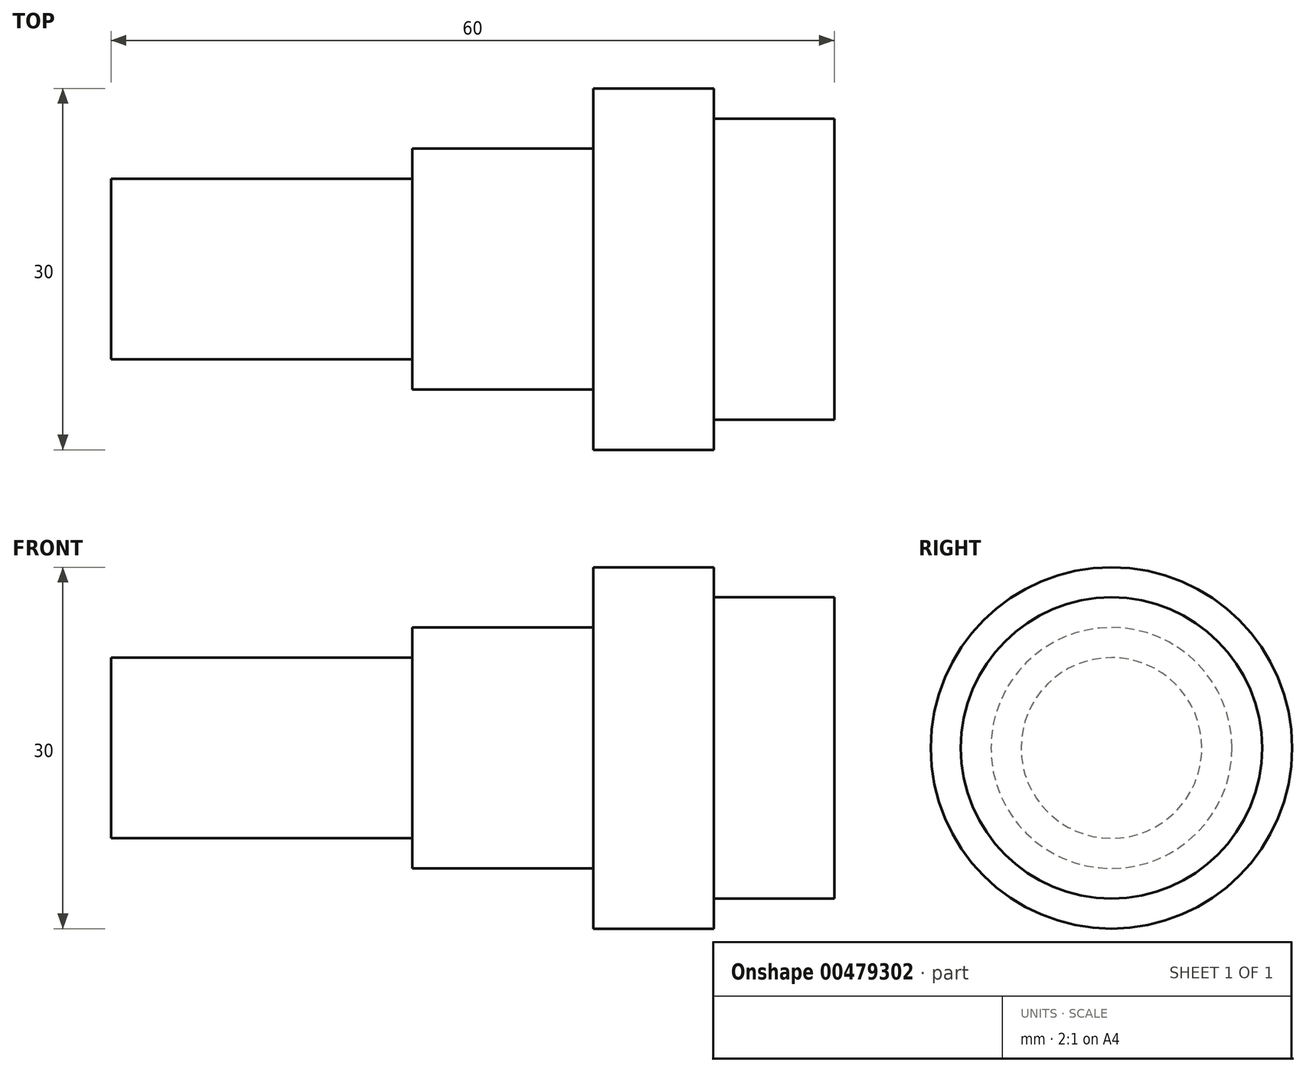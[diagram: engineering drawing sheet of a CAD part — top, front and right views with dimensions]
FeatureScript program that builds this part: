
annotation { "Feature Type Name" : "Feature", "Feature Type Description" : "" }
export const myFeature = defineFeature(function(context is Context, id is Id, definition is map)
    precondition{}
    {
        {
            var Q0;
            Q0=qCreatedBy(makeId("Right.planeOp"),FACE);
            var sketch = newSketch(context, id + "F0", { "sketchPlane" : qUnion([Q0])});
            skCircle(sketch, "E0", {"center": v(0, 0) * mm, "radius": 12.5 * mm});
            skSolve(sketch);
        }
        {
            var Q0;
            Q0 = qSketchRegion(id + "F0", true);
            extrude(context, id + "F1", {"entities" : qUnion([Q0]), "depth" : 10 * mm});
        }
        {
            var Q0;
            Q0=makeQuery(id+"F1.opExtrude","CAP_FACE",FACE,{"disambiguationData":[OSD([sQuery(id+"F0.wireOp",EDGE,"E0")])],"isStart":true});
            var sketch = newSketch(context, id + "F2", { "sketchPlane" : qUnion([Q0])});
            skCircle(sketch, "E1", {"center": v(0, 0) * mm, "radius": 15 * mm});
            skSolve(sketch);
        }
        {
            var Q0;
            Q0 = qSketchRegion(id + "F2", true);
            extrude(context, id + "F3", {"entities" : qUnion([Q0]), "operationType" : NewBodyOperationType.ADD, "depth" : 10 * mm});
        }
        {
            var Q0;
            Q0=makeQuery(id+"F3.opExtrude","CAP_FACE",FACE,{"disambiguationData":[OSD([sQuery(id+"F2.wireOp",EDGE,"E1")])],"isStart":false});
            var sketch = newSketch(context, id + "F4", { "sketchPlane" : qUnion([Q0])});
            skCircle(sketch, "E2", {"center": v(0, 0) * mm, "radius": 10 * mm});
            skSolve(sketch);
        }
        {
            var Q0;
            Q0 = qSketchRegion(id + "F4", true);
            extrude(context, id + "F5", {"entities" : qUnion([Q0]), "operationType" : NewBodyOperationType.ADD, "depth" : 15 * mm});
        }
        {
            var Q0;
            Q0=makeQuery(id+"F5.opExtrude","CAP_FACE",FACE,{"disambiguationData":[OSD([sQuery(id+"F4.wireOp",EDGE,"E2")])],"isStart":false});
            var sketch = newSketch(context, id + "F6", { "sketchPlane" : qUnion([Q0])});
            skCircle(sketch, "E3", {"center": v(0, 0) * mm, "radius": 7.5 * mm});
            skSolve(sketch);
        }
        {
            var Q0;
            Q0 = qSketchRegion(id + "F6", true);
            extrude(context, id + "F7", {"entities" : qUnion([Q0]), "operationType" : NewBodyOperationType.ADD, "depth" : 25 * mm});
        }
    });
